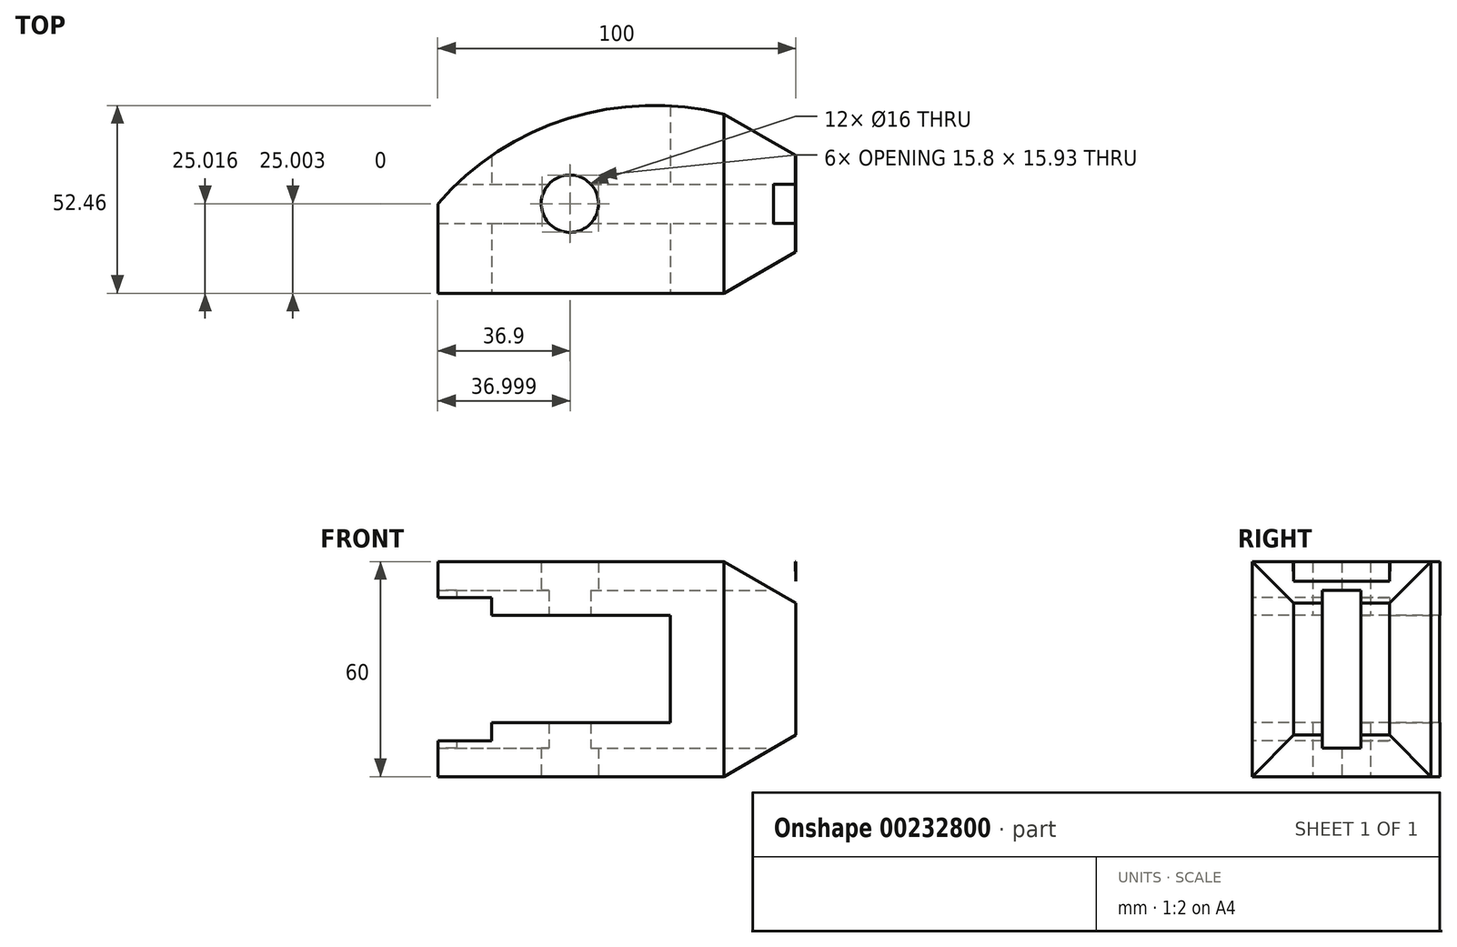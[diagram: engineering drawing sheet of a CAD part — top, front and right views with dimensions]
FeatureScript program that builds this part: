
annotation { "Feature Type Name" : "Feature", "Feature Type Description" : "" }
export const myFeature = defineFeature(function(context is Context, id is Id, definition is map)
    precondition{}
    {
        {
            var Q0;
            Q0=qCreatedBy(makeId("Top.planeOp"),FACE);
            var sketch = newSketch(context, id + "F0", { "sketchPlane" : qUnion([Q0])});
            skArc(sketch, "E0", {"start": v(19.67, 77.54) * mm, "mid": v(-23.86, 76.36) * mm, "end": v(-60.33, 52.54) * mm});
            skLineSegment(sketch, "E1", {"start": v(-60.33, 52.54) * mm, "end": v(-60.33, 27.54) * mm});
            skLineSegment(sketch, "E2", {"start": v(-60.33, 27.54) * mm, "end": v(19.67, 27.54) * mm});
            skLineSegment(sketch, "E3", {"start": v(19.67, 27.54) * mm, "end": v(19.67, 77.54) * mm});
            skCircle(sketch, "E4", {"center": v(-23.43, 52.54) * mm, "radius": 8 * mm});
            skLineSegment(sketch, "E5", {"start": v(19.67, 27.54) * mm, "end": v(61.5, 27.54) * mm, "construction": true});
            skLineSegment(sketch, "E6", {"start": v(19.67, 27.54) * mm, "end": v(39.67, 39.1) * mm});
            skLineSegment(sketch, "E7", {"start": v(39.67, 39.1) * mm, "end": v(39.67, 66) * mm});
            skLineSegment(sketch, "E8", {"start": v(39.67, 66) * mm, "end": v(19.67, 77.54) * mm});
            skSolve(sketch);
        }
        {
            var Q0;
            Q0=makeQuery(id+"F0.imprint","IMPRINT",FACE,{"disambiguationData":[TD([[makeQuery(id+"F0.imprint","IMPRINT",EDGE,{"derivedFrom":sQuery(id+"F0.wireOp",EDGE,"E0")}),1.0]])]});
            var Q1;
            Q1=makeQuery(id+"F0.imprint","IMPRINT",FACE,{"disambiguationData":[TD([[makeQuery(id+"F0.imprint","IMPRINT",EDGE,{"derivedFrom":sQuery(id+"F0.wireOp",EDGE,"E3")}),-1.0]])]});
            extrude(context, id + "F1", {"entities" : qUnion([Q0, Q1]), "depth" : 60 * mm});
        }
        {
            var Q0;
            Q0=makeQuery(id+"F1.opExtrude","SWEPT_FACE",FACE,{"disambiguationData":[OSD([sQuery(id+"F0.wireOp",EDGE,"E7")])]});
            var sketch = newSketch(context, id + "F2", { "sketchPlane" : qUnion([Q0])});
            skLineSegment(sketch, "E9.bottom", {"start": v(58, 52) * mm, "end": v(47.1, 52) * mm});
            skLineSegment(sketch, "E9.top", {"start": v(58, 8) * mm, "end": v(47.1, 8) * mm});
            skLineSegment(sketch, "E9.left", {"start": v(58, 52) * mm, "end": v(58, 8) * mm});
            skLineSegment(sketch, "E9.right", {"start": v(47.1, 52) * mm, "end": v(47.1, 8) * mm});
            skPoint(sketch, "E9.middle", {"position": v(52.54, 30) * mm});
            skLineSegment(sketch, "E10", {"start": v(66, 60) * mm, "end": v(39.1, 60) * mm, "construction": true});
            skLineSegment(sketch, "E11", {"start": v(39.1, 60) * mm, "end": v(39.1, 0) * mm, "construction": true});
            skLineSegment(sketch, "E12", {"start": v(39.1, 0) * mm, "end": v(66, 0) * mm, "construction": true});
            skLineSegment(sketch, "E13", {"start": v(66, 0) * mm, "end": v(66, 60) * mm, "construction": true});
            skSolve(sketch);
        }
        {
            var Q0;
            Q0=makeQuery(id+"F2.imprint","IMPRINT",FACE,{"disambiguationData":[TD([[makeQuery(id+"F2.imprint","IMPRINT",EDGE,{"derivedFrom":sQuery(id+"F2.wireOp",EDGE,"E9.bottom")}),1.0]])]});
            var Q1;
            Q1 = qSketchRegion(id + "F4", true);
            extrude(context, id + "F3", {"entities" : qUnion([Q0, Q1]), "operationType" : NewBodyOperationType.REMOVE, "endBound" : BoundingType.THROUGH_ALL, "oppositeDirection" : true, "depth" : 25 * mm});
        }
        {
            var Q0;
            Q0=makeQuery(id+"F1.opExtrude","SWEPT_FACE",FACE,{"disambiguationData":[OSD([sQuery(id+"F0.wireOp",EDGE,"E2")])]});
            var sketch = newSketch(context, id + "F4", { "sketchPlane" : qUnion([Q0])});
            skLineSegment(sketch, "E14", {"start": v(-60.33, 60) * mm, "end": v(-60.33, 0) * mm, "construction": true});
            skLineSegment(sketch, "E15", {"start": v(-60.33, 0) * mm, "end": v(19.67, 0) * mm, "construction": true});
            skLineSegment(sketch, "E16", {"start": v(19.67, 0) * mm, "end": v(19.67, 60) * mm, "construction": true});
            skLineSegment(sketch, "E17", {"start": v(19.67, 60) * mm, "end": v(-60.33, 60) * mm, "construction": true});
            skLineSegment(sketch, "E18", {"start": v(-60.33, 10) * mm, "end": v(-45.33, 10) * mm});
            skLineSegment(sketch, "E19", {"start": v(-45.33, 10) * mm, "end": v(-45.33, 15) * mm});
            skLineSegment(sketch, "E20", {"start": v(-45.33, 15) * mm, "end": v(4.67, 15) * mm});
            skLineSegment(sketch, "E21", {"start": v(4.67, 15) * mm, "end": v(4.67, 30) * mm});
            skLineSegment(sketch, "E22.MirrorCS", {"start": v(4.67, 45) * mm, "end": v(4.67, 30) * mm});
            skLineSegment(sketch, "E23.MirrorCS", {"start": v(-45.33, 45) * mm, "end": v(4.67, 45) * mm});
            skLineSegment(sketch, "E24.MirrorCS", {"start": v(-60.33, 50) * mm, "end": v(-45.33, 50) * mm});
            skLineSegment(sketch, "E25.MirrorCS", {"start": v(-45.33, 50) * mm, "end": v(-45.33, 45) * mm});
            skLineSegment(sketch, "E26", {"start": v(19.67, 60) * mm, "end": v(39.81, 48.32) * mm});
            skLineSegment(sketch, "E27", {"start": v(19.67, 0) * mm, "end": v(39.81, 11.68) * mm});
            skLineSegment(sketch, "E28", {"start": v(19.67, 60) * mm, "end": v(39.55, 60) * mm});
            skLineSegment(sketch, "E29", {"start": v(39.55, 60) * mm, "end": v(39.81, 48.32) * mm});
            skLineSegment(sketch, "E30", {"start": v(39.81, 11.68) * mm, "end": v(39.81, 0) * mm});
            skLineSegment(sketch, "E31", {"start": v(39.81, 0) * mm, "end": v(19.67, 0) * mm});
            skSolve(sketch);
        }
        {
            var Q0;
            {var subQ1=sQuery(id+"F4.wireOp",EDGE,"E18");Q0=makeQuery(id+"F4.imprint","IMPRINT",FACE,{"disambiguationData":[TD([[makeQuery(id+"F4.imprint","IMPRINT",EDGE,{"derivedFrom":subQ1}),1.0]])]});}
            var Q1;
            Q1=makeQuery(id+"F4.imprint","IMPRINT",FACE,{"disambiguationData":[TD([[makeQuery(id+"F4.imprint","IMPRINT",EDGE,{"derivedFrom":sQuery(id+"F4.wireOp",EDGE,"E26")}),1.0]])]});
            var Q2;
            Q2=makeQuery(id+"F4.imprint","IMPRINT",FACE,{"disambiguationData":[TD([[makeQuery(id+"F4.imprint","IMPRINT",EDGE,{"derivedFrom":sQuery(id+"F4.wireOp",EDGE,"E27")}),-1.0]])]});
            extrude(context, id + "F5", {"entities" : qUnion([Q0, Q1, Q2]), "operationType" : NewBodyOperationType.REMOVE, "endBound" : BoundingType.THROUGH_ALL, "oppositeDirection" : true, "depth" : 25 * mm});
        }
    });
